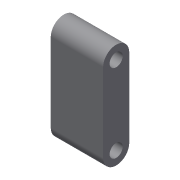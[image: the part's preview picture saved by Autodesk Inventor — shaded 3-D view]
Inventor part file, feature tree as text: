
AUTODESK INVENTOR PART (.ipt)
format: ipt  version: 2015 (Build 190159000, 159)  size: 82,944 bytes
history: native  units: mm
features: extrude x1, sketch x1
ambient origin geometry x8: Origin, YZ Plane, XZ Plane, XY Plane, X Axis, Y Axis, Z Axis, Center Point
bodies: Body1 (feature_tree)
feature tree (2):
  extrude  "Extrusion2"  Depth=0.5mm
  sketch  "Sketch2"  dims[d7=1.0mm d8=0.5mm d10=0.5mm d11=1.0mm d12=2.0mm d13=0.0mm]
